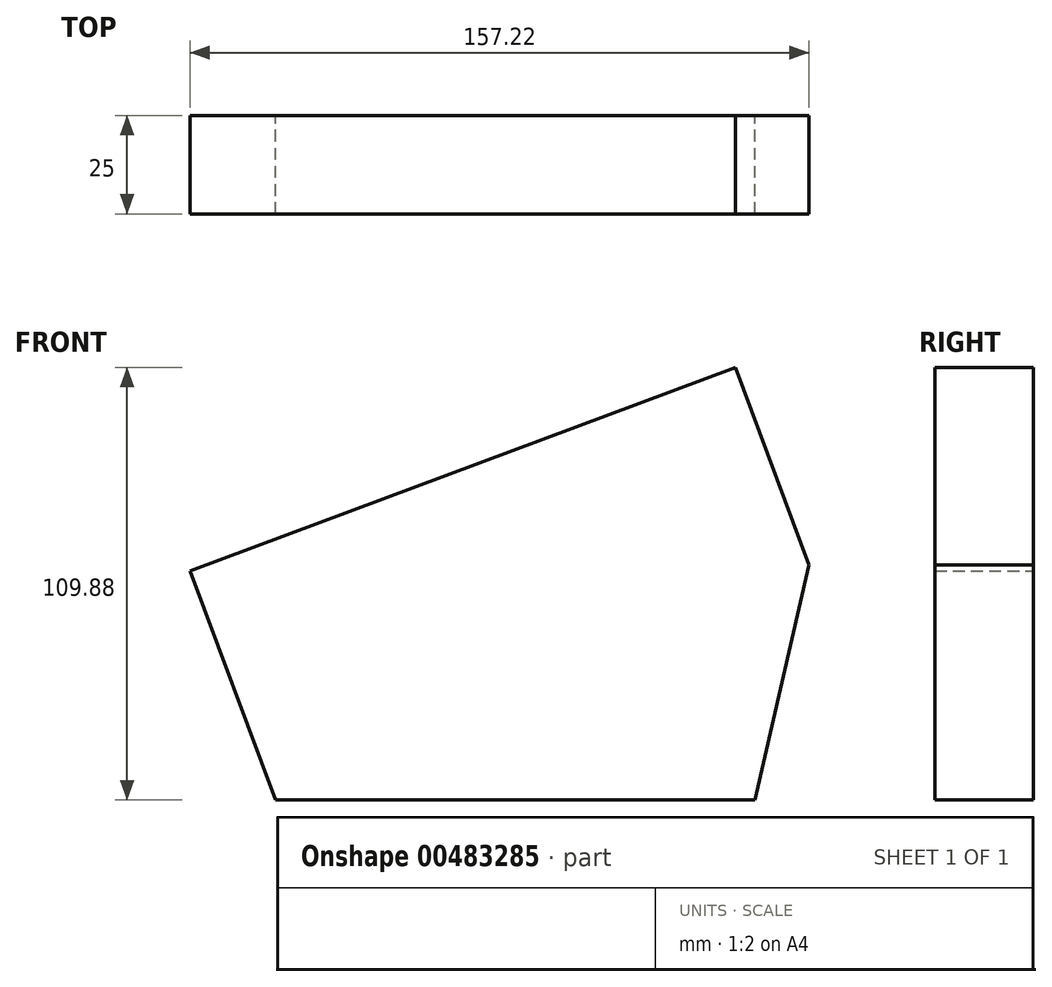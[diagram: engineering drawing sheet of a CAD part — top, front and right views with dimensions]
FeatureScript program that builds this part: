
annotation { "Feature Type Name" : "Feature", "Feature Type Description" : "" }
export const myFeature = defineFeature(function(context is Context, id is Id, definition is map)
    precondition{}
    {
        {
            var Q0;
            Q0=qCreatedBy(makeId("Front.planeOp"),FACE);
            var sketch = newSketch(context, id + "F0", { "sketchPlane" : qUnion([Q0])});
            skLineSegment(sketch, "E0", {"start": v(-72.45, 2.75) * mm, "end": v(66.04, 54.48) * mm});
            skLineSegment(sketch, "E1", {"start": v(66.04, 54.48) * mm, "end": v(84.77, 4.36) * mm});
            skLineSegment(sketch, "E2", {"start": v(71.08, -55.4) * mm, "end": v(-50.73, -55.4) * mm});
            skLineSegment(sketch, "E3", {"start": v(-50.73, -55.4) * mm, "end": v(-72.45, 2.75) * mm});
            skLineSegment(sketch, "E4", {"start": v(84.77, 4.36) * mm, "end": v(71.08, -55.4) * mm});
            skSolve(sketch);
        }
        {
            var Q0;
            Q0=makeQuery(id+"F0.imprint","IMPRINT",FACE,{"disambiguationData":[TD([[makeQuery(id+"F0.imprint","IMPRINT",EDGE,{"derivedFrom":sQuery(id+"F0.wireOp",EDGE,"E0")}),-1.0]])]});
            extrude(context, id + "F1", {"entities" : qUnion([Q0]), "depth" : 25 * mm, "offsetDistance" : 25 * mm});
        }
    });
